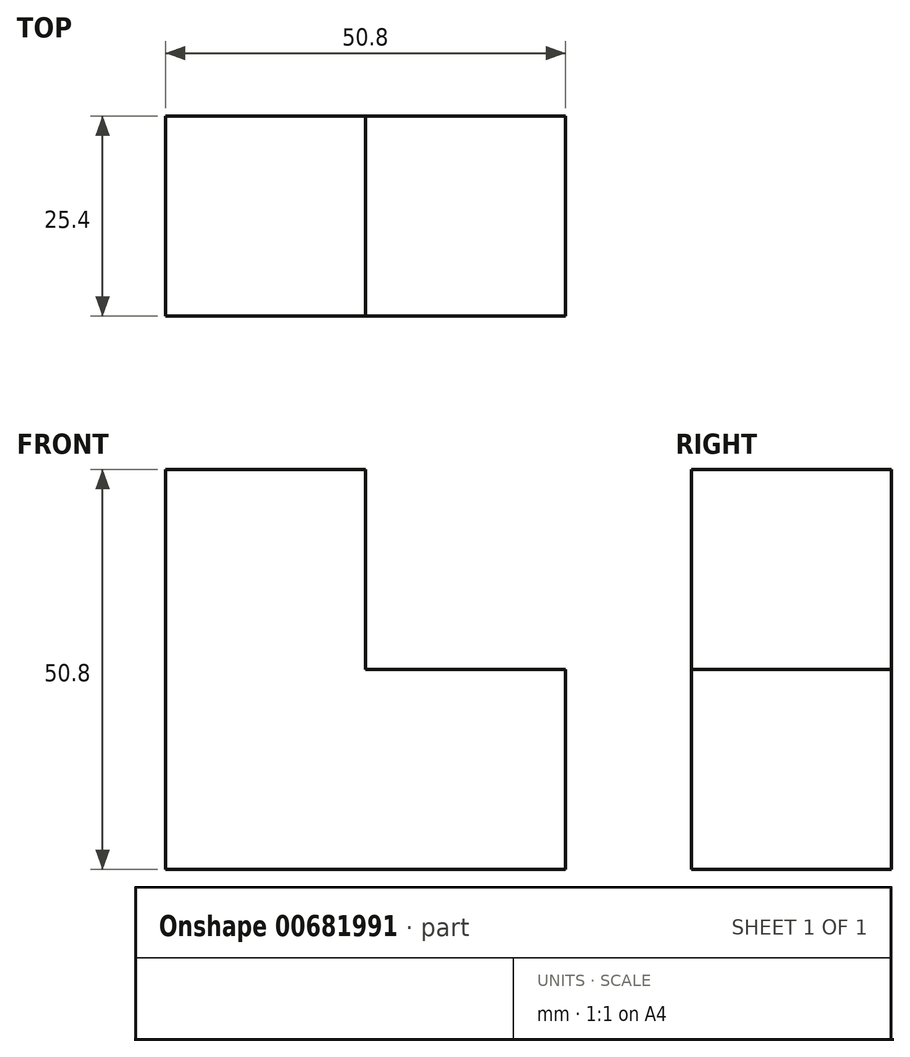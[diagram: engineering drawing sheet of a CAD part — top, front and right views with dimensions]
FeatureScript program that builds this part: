
annotation { "Feature Type Name" : "Feature", "Feature Type Description" : "" }
export const myFeature = defineFeature(function(context is Context, id is Id, definition is map)
    precondition{}
    {
        {
            var Q0;
            Q0=qCreatedBy(makeId("Front.planeOp"),FACE);
            var sketch = newSketch(context, id + "F0", { "sketchPlane" : qUnion([Q0])});
            skLineSegment(sketch, "E0", {"start": v(0, 0) * mm, "end": v(-50.8, 0) * mm});
            skLineSegment(sketch, "E1", {"start": v(-50.8, 0) * mm, "end": v(-50.8, 50.8) * mm});
            skLineSegment(sketch, "E2", {"start": v(-50.8, 50.8) * mm, "end": v(-25.4, 50.8) * mm});
            skLineSegment(sketch, "E3", {"start": v(-25.4, 50.8) * mm, "end": v(-25.4, 25.4) * mm});
            skLineSegment(sketch, "E4", {"start": v(-25.4, 25.4) * mm, "end": v(0, 25.4) * mm});
            skLineSegment(sketch, "E5", {"start": v(0, 25.4) * mm, "end": v(0, 0) * mm});
            skSolve(sketch);
        }
        {
            var Q0;
            Q0 = qSketchRegion(id + "F0", true);
            extrude(context, id + "F1", {"entities" : qUnion([Q0]), "depth" : 25.4 * mm, "offsetDistance" : 25.4 * mm});
        }
    });
